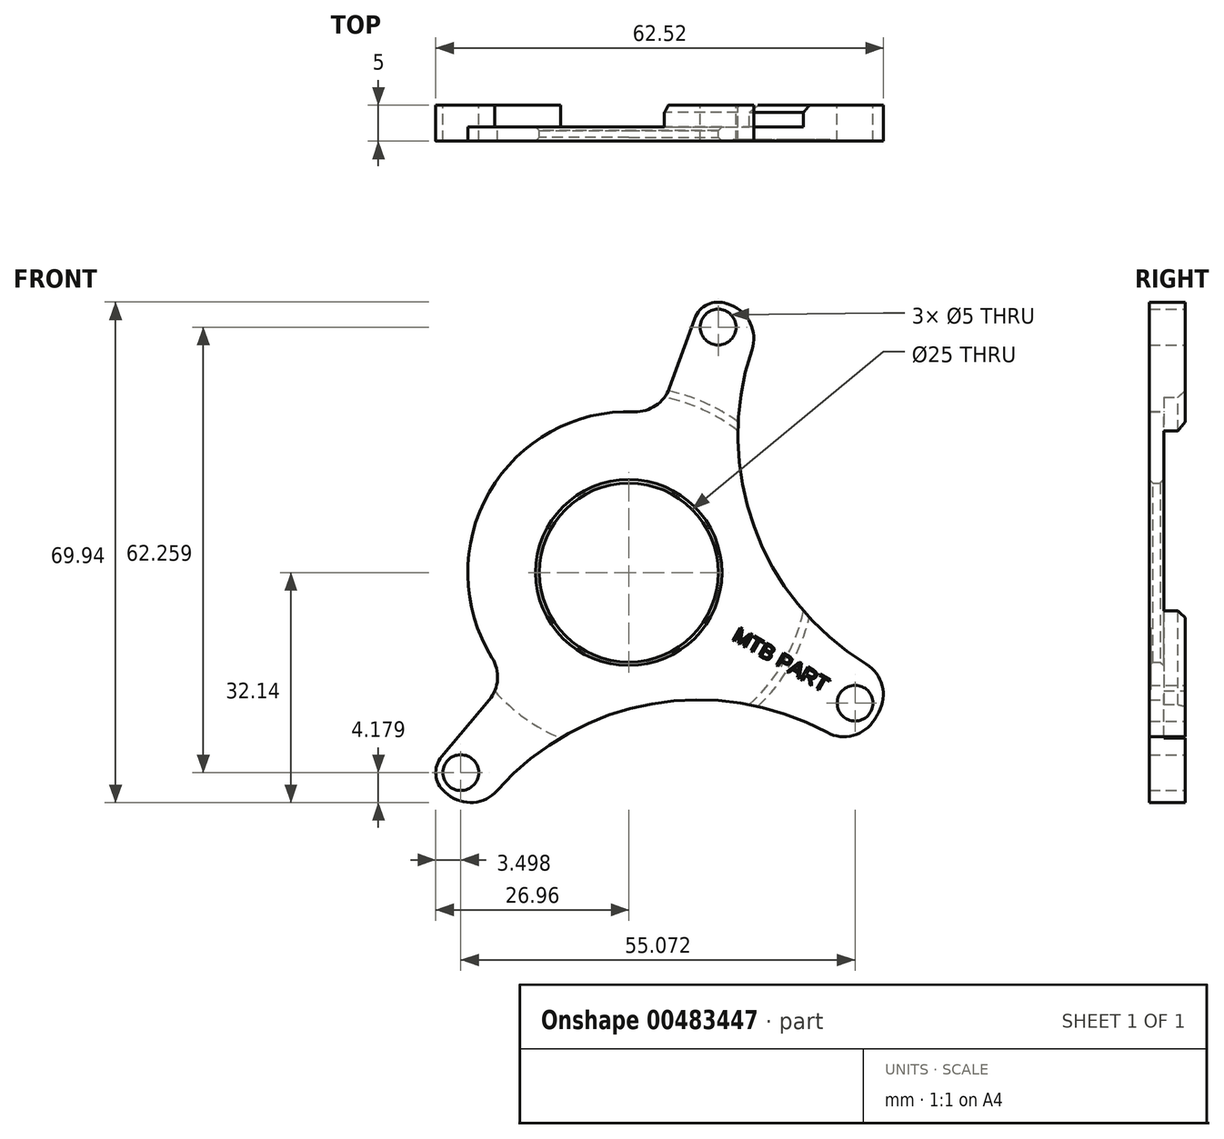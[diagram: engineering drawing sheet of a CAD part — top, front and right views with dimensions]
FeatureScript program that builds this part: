
annotation { "Feature Type Name" : "Feature", "Feature Type Description" : "" }
export const myFeature = defineFeature(function(context is Context, id is Id, definition is map)
    precondition{}
    {
        {
            var Q0;
            Q0=qCreatedBy(makeId("Front.planeOp"),FACE);
            var sketch = newSketch(context, id + "F0", { "sketchPlane" : qUnion([Q0])});
            skCircle(sketch, "E0", {"center": v(0, 0) * mm, "radius": 12.5 * mm});
            skArc(sketch, "E1", {"start": v(-25.71, -30.64) * mm, "mid": v(-25.49, -30.83) * mm, "end": v(-25.26, -31.01) * mm});
            skLineSegment(sketch, "E2", {"start": v(0, 0) * mm, "end": v(-23.46, -27.96) * mm, "construction": true});
            skLineSegment(sketch, "E3", {"start": v(0, 0) * mm, "end": v(31.6, -18.25) * mm, "construction": true});
            skLineSegment(sketch, "E4", {"start": v(0, 0) * mm, "end": v(12.48, 34.3) * mm, "construction": true});
            skCircle(sketch, "E5", {"center": v(0, 0) * mm, "radius": 36.5 * mm, "construction": true});
            skCircle(sketch, "E6", {"center": v(12.48, 34.3) * mm, "radius": 2.5 * mm});
            skCircle(sketch, "E7", {"center": v(31.6, -18.25) * mm, "radius": 2.5 * mm});
            skCircle(sketch, "E8", {"center": v(-23.46, -27.96) * mm, "radius": 2.5 * mm});
            skArc(sketch, "E9", {"start": v(0.78, 22.49) * mm, "mid": v(-19.49, 11.25) * mm, "end": v(-19.08, -11.92) * mm});
            skArc(sketch, "E10", {"start": v(13.68, 37.59) * mm, "mid": v(10.93, 37.43) * mm, "end": v(9.14, 35.34) * mm});
            skArc(sketch, "E11", {"start": v(-26.03, -25.58) * mm, "mid": v(-26.95, -28.18) * mm, "end": v(-25.71, -30.64) * mm});
            skLineSegment(sketch, "E12", {"start": v(-26.14, -25.71) * mm, "end": v(-19.5, -17.78) * mm});
            skLineSegment(sketch, "E13", {"start": v(9.2, 35.5) * mm, "end": v(5.66, 25.77) * mm});
            skPoint(sketch, "E14.visualSharp", {"position": v(4.31, 22.08) * mm});
            skArc(sketch, "E14.filletArc", {"start": v(0.78, 22.49) * mm, "mid": v(3.75, 23.34) * mm, "end": v(5.66, 25.77) * mm});
            skPoint(sketch, "E15.visualSharp", {"position": v(-16.97, -14.78) * mm});
            skArc(sketch, "E15.filletArc", {"start": v(-19.5, -17.78) * mm, "mid": v(-18.33, -14.92) * mm, "end": v(-19.08, -11.92) * mm});
            skArc(sketch, "E16", {"start": v(17.2, 31.12) * mm, "mid": v(17.5, 6.37) * mm, "end": v(33.17, -12.79) * mm});
            skArc(sketch, "E17", {"start": v(27.66, -22.33) * mm, "mid": v(3.24, -18.35) * mm, "end": v(-18.36, -30.45) * mm});
            skArc(sketch, "E18.trimOffspring", {"start": v(14.23, 37.38) * mm, "mid": v(13.96, 37.49) * mm, "end": v(13.68, 37.59) * mm});
            skArc(sketch, "E19.trimOffspring", {"start": v(34.34, -20.5) * mm, "mid": v(34.64, -20) * mm, "end": v(34.93, -19.5) * mm});
            skPoint(sketch, "E20.visualSharp", {"position": v(18.86, 35.27) * mm});
            skArc(sketch, "E20.filletArc", {"start": v(17.2, 31.12) * mm, "mid": v(16.97, 34.85) * mm, "end": v(14.23, 37.38) * mm});
            skPoint(sketch, "E21.visualSharp", {"position": v(37.12, -14.9) * mm});
            skArc(sketch, "E21.filletArc", {"start": v(34.93, -19.5) * mm, "mid": v(35.4, -15.79) * mm, "end": v(33.17, -12.79) * mm});
            skPoint(sketch, "E22.visualSharp", {"position": v(31.46, -24.7) * mm});
            skArc(sketch, "E22.filletArc", {"start": v(27.66, -22.33) * mm, "mid": v(31.37, -22.76) * mm, "end": v(34.34, -20.5) * mm});
            skPoint(sketch, "E23.visualSharp", {"position": v(-21.11, -33.97) * mm});
            skArc(sketch, "E23.filletArc", {"start": v(-25.26, -31.01) * mm, "mid": v(-21.7, -32.12) * mm, "end": v(-18.36, -30.45) * mm});
            skSolve(sketch);
        }
        {
            var Q0;
            Q0 = qSketchRegion(id + "F0", true);
            extrude(context, id + "F1", {"entities" : qUnion([Q0]), "depth" : 5 * mm});
        }
        {
            var Q0;
            Q0=makeQuery(id+"F1.opExtrude","CAP_FACE",FACE,{"disambiguationData":[OSD([sQuery(id+"F0.wireOp",EDGE,"E0"),sQuery(id+"F0.wireOp",EDGE,"E1"),sQuery(id+"F0.wireOp",EDGE,"E6"),sQuery(id+"F0.wireOp",EDGE,"E7"),sQuery(id+"F0.wireOp",EDGE,"E8"),sQuery(id+"F0.wireOp",EDGE,"E9"),sQuery(id+"F0.wireOp",EDGE,"E10"),sQuery(id+"F0.wireOp",EDGE,"E11"),sQuery(id+"F0.wireOp",EDGE,"E12"),sQuery(id+"F0.wireOp",EDGE,"E13"),sQuery(id+"F0.wireOp",EDGE,"E14.filletArc"),sQuery(id+"F0.wireOp",EDGE,"E15.filletArc"),sQuery(id+"F0.wireOp",EDGE,"E16"),sQuery(id+"F0.wireOp",EDGE,"E17"),sQuery(id+"F0.wireOp",EDGE,"E18.trimOffspring"),sQuery(id+"F0.wireOp",EDGE,"E19.trimOffspring"),sQuery(id+"F0.wireOp",EDGE,"E20.filletArc"),sQuery(id+"F0.wireOp",EDGE,"E21.filletArc"),sQuery(id+"F0.wireOp",EDGE,"E22.filletArc"),sQuery(id+"F0.wireOp",EDGE,"E23.filletArc")])],"isStart":true});
            var sketch = newSketch(context, id + "F2", { "sketchPlane" : qUnion([Q0])});
            skCircle(sketch, "E24", {"center": v(0, 0) * mm, "radius": 25 * mm});
            skSolve(sketch);
        }
        {
            var Q0;
            Q0 = qSketchRegion(id + "F2", true);
            extrude(context, id + "F3", {"entities" : qUnion([Q0]), "operationType" : NewBodyOperationType.REMOVE, "oppositeDirection" : true, "depth" : 3 * mm});
        }
        {
            var Q0;
            {var subQ0=sQuery(id+"F0.wireOp",EDGE,"E16");var subQ1=sQuery(id+"F0.wireOp",EDGE,"E14.filletArc");var subQ2=sQuery(id+"F2.wireOp",EDGE,"E24");Q0=makeQuery(id+"F3.boolean.opBoolean","COPY",EDGE,{"disambiguationData":[TD([makeQuery(id+"F1.opExtrude","CAP_FACE",FACE,{"disambiguationData":[OSD([sQuery(id+"F0.wireOp",EDGE,"E0"),sQuery(id+"F0.wireOp",EDGE,"E1"),sQuery(id+"F0.wireOp",EDGE,"E6"),sQuery(id+"F0.wireOp",EDGE,"E7"),sQuery(id+"F0.wireOp",EDGE,"E8"),sQuery(id+"F0.wireOp",EDGE,"E9"),sQuery(id+"F0.wireOp",EDGE,"E10"),sQuery(id+"F0.wireOp",EDGE,"E11"),sQuery(id+"F0.wireOp",EDGE,"E12"),sQuery(id+"F0.wireOp",EDGE,"E13"),subQ1,sQuery(id+"F0.wireOp",EDGE,"E15.filletArc"),subQ0,sQuery(id+"F0.wireOp",EDGE,"E17"),sQuery(id+"F0.wireOp",EDGE,"E18.trimOffspring"),sQuery(id+"F0.wireOp",EDGE,"E19.trimOffspring"),sQuery(id+"F0.wireOp",EDGE,"E20.filletArc"),sQuery(id+"F0.wireOp",EDGE,"E21.filletArc"),sQuery(id+"F0.wireOp",EDGE,"E22.filletArc"),sQuery(id+"F0.wireOp",EDGE,"E23.filletArc")])],"isStart":true}),makeQuery(id+"F1.opExtrude","SWEPT_FACE",FACE,{"disambiguationData":[OSD([subQ1])]}),makeQuery(id+"F1.opExtrude","SWEPT_FACE",FACE,{"disambiguationData":[OSD([subQ0])]}),makeQuery(id+"F3.opExtrude","SWEPT_FACE",FACE,{"disambiguationData":[OSD([subQ2])]})])],"derivedFrom":makeQuery(id+"F3.opExtrude","CAP_EDGE",EDGE,{"disambiguationData":[OSD([subQ2])],"isStart":true})});}
            var Q1;
            {var subQ0=sQuery(id+"F0.wireOp",EDGE,"E17");var subQ1=sQuery(id+"F0.wireOp",EDGE,"E16");var subQ2=sQuery(id+"F2.wireOp",EDGE,"E24");Q1=makeQuery(id+"F3.boolean.opBoolean","COPY",EDGE,{"disambiguationData":[TD([makeQuery(id+"F1.opExtrude","CAP_FACE",FACE,{"disambiguationData":[OSD([sQuery(id+"F0.wireOp",EDGE,"E0"),sQuery(id+"F0.wireOp",EDGE,"E1"),sQuery(id+"F0.wireOp",EDGE,"E6"),sQuery(id+"F0.wireOp",EDGE,"E7"),sQuery(id+"F0.wireOp",EDGE,"E8"),sQuery(id+"F0.wireOp",EDGE,"E9"),sQuery(id+"F0.wireOp",EDGE,"E10"),sQuery(id+"F0.wireOp",EDGE,"E11"),sQuery(id+"F0.wireOp",EDGE,"E12"),sQuery(id+"F0.wireOp",EDGE,"E13"),sQuery(id+"F0.wireOp",EDGE,"E14.filletArc"),sQuery(id+"F0.wireOp",EDGE,"E15.filletArc"),subQ1,subQ0,sQuery(id+"F0.wireOp",EDGE,"E18.trimOffspring"),sQuery(id+"F0.wireOp",EDGE,"E19.trimOffspring"),sQuery(id+"F0.wireOp",EDGE,"E20.filletArc"),sQuery(id+"F0.wireOp",EDGE,"E21.filletArc"),sQuery(id+"F0.wireOp",EDGE,"E22.filletArc"),sQuery(id+"F0.wireOp",EDGE,"E23.filletArc")])],"isStart":true}),makeQuery(id+"F1.opExtrude","SWEPT_FACE",FACE,{"disambiguationData":[OSD([subQ1])]}),makeQuery(id+"F1.opExtrude","SWEPT_FACE",FACE,{"disambiguationData":[OSD([subQ0])]}),makeQuery(id+"F3.opExtrude","SWEPT_FACE",FACE,{"disambiguationData":[OSD([subQ2])]})])],"derivedFrom":makeQuery(id+"F3.opExtrude","CAP_EDGE",EDGE,{"disambiguationData":[OSD([subQ2])],"isStart":true})});}
            var Q2;
            {var subQ0=sQuery(id+"F0.wireOp",EDGE,"E17");var subQ1=sQuery(id+"F0.wireOp",EDGE,"E15.filletArc");var subQ2=sQuery(id+"F2.wireOp",EDGE,"E24");Q2=makeQuery(id+"F3.boolean.opBoolean","COPY",EDGE,{"disambiguationData":[TD([makeQuery(id+"F1.opExtrude","CAP_FACE",FACE,{"disambiguationData":[OSD([sQuery(id+"F0.wireOp",EDGE,"E0"),sQuery(id+"F0.wireOp",EDGE,"E1"),sQuery(id+"F0.wireOp",EDGE,"E6"),sQuery(id+"F0.wireOp",EDGE,"E7"),sQuery(id+"F0.wireOp",EDGE,"E8"),sQuery(id+"F0.wireOp",EDGE,"E9"),sQuery(id+"F0.wireOp",EDGE,"E10"),sQuery(id+"F0.wireOp",EDGE,"E11"),sQuery(id+"F0.wireOp",EDGE,"E12"),sQuery(id+"F0.wireOp",EDGE,"E13"),sQuery(id+"F0.wireOp",EDGE,"E14.filletArc"),subQ1,sQuery(id+"F0.wireOp",EDGE,"E16"),subQ0,sQuery(id+"F0.wireOp",EDGE,"E18.trimOffspring"),sQuery(id+"F0.wireOp",EDGE,"E19.trimOffspring"),sQuery(id+"F0.wireOp",EDGE,"E20.filletArc"),sQuery(id+"F0.wireOp",EDGE,"E21.filletArc"),sQuery(id+"F0.wireOp",EDGE,"E22.filletArc"),sQuery(id+"F0.wireOp",EDGE,"E23.filletArc")])],"isStart":true}),makeQuery(id+"F1.opExtrude","SWEPT_FACE",FACE,{"disambiguationData":[OSD([subQ1])]}),makeQuery(id+"F1.opExtrude","SWEPT_FACE",FACE,{"disambiguationData":[OSD([subQ0])]}),makeQuery(id+"F3.opExtrude","SWEPT_FACE",FACE,{"disambiguationData":[OSD([subQ2])]})])],"derivedFrom":makeQuery(id+"F3.opExtrude","CAP_EDGE",EDGE,{"disambiguationData":[OSD([subQ2])],"isStart":true})});}
            chamfer(context, id + "F4", {"entities" : qUnion([Q0, Q1, Q2]), "width" : 1 * mm, "tangentPropagation" : true});
        }
        {
            var Q0;
            Q0=makeQuery(id+"F1.opExtrude","SWEPT_FACE",FACE,{"disambiguationData":[OSD([sQuery(id+"F0.wireOp",EDGE,"E0")])]});
            chamfer(context, id + "F5", {"entities" : qUnion([Q0]), "width" : 0.5 * mm, "tangentPropagation" : true});
        }
        {
            var Q0;
            Q0=makeQuery(id+"F1.opExtrude","CAP_FACE",FACE,{"disambiguationData":[OSD([sQuery(id+"F0.wireOp",EDGE,"E0"),sQuery(id+"F0.wireOp",EDGE,"E1"),sQuery(id+"F0.wireOp",EDGE,"E6"),sQuery(id+"F0.wireOp",EDGE,"E7"),sQuery(id+"F0.wireOp",EDGE,"E8"),sQuery(id+"F0.wireOp",EDGE,"E9"),sQuery(id+"F0.wireOp",EDGE,"E10"),sQuery(id+"F0.wireOp",EDGE,"E11"),sQuery(id+"F0.wireOp",EDGE,"E12"),sQuery(id+"F0.wireOp",EDGE,"E13"),sQuery(id+"F0.wireOp",EDGE,"E14.filletArc"),sQuery(id+"F0.wireOp",EDGE,"E15.filletArc"),sQuery(id+"F0.wireOp",EDGE,"E16"),sQuery(id+"F0.wireOp",EDGE,"E17"),sQuery(id+"F0.wireOp",EDGE,"E18.trimOffspring"),sQuery(id+"F0.wireOp",EDGE,"E19.trimOffspring"),sQuery(id+"F0.wireOp",EDGE,"E20.filletArc"),sQuery(id+"F0.wireOp",EDGE,"E21.filletArc"),sQuery(id+"F0.wireOp",EDGE,"E22.filletArc"),sQuery(id+"F0.wireOp",EDGE,"E23.filletArc")])],"isStart":false});
            var sketch = newSketch(context, id + "F6", { "sketchPlane" : qUnion([Q0])});
            skText(sketch, "E25", { "text": "MTB PART\n", "fontName": "Arimo-Regular.ttf"});
            const initialGuessF6  = {"E25": [0.01432, -0.00934, 0.86603, -0.5, 0.00212]};
            skSetInitialGuess(sketch, initialGuessF6);
            skSolve(sketch);
        }
        {
            var Q0;
            Q0 = qSketchRegion(id + "F6", true);
            extrude(context, id + "F7", {"entities" : qUnion([Q0]), "operationType" : NewBodyOperationType.REMOVE, "oppositeDirection" : true, "depth" : 0.2 * mm});
        }
    });
